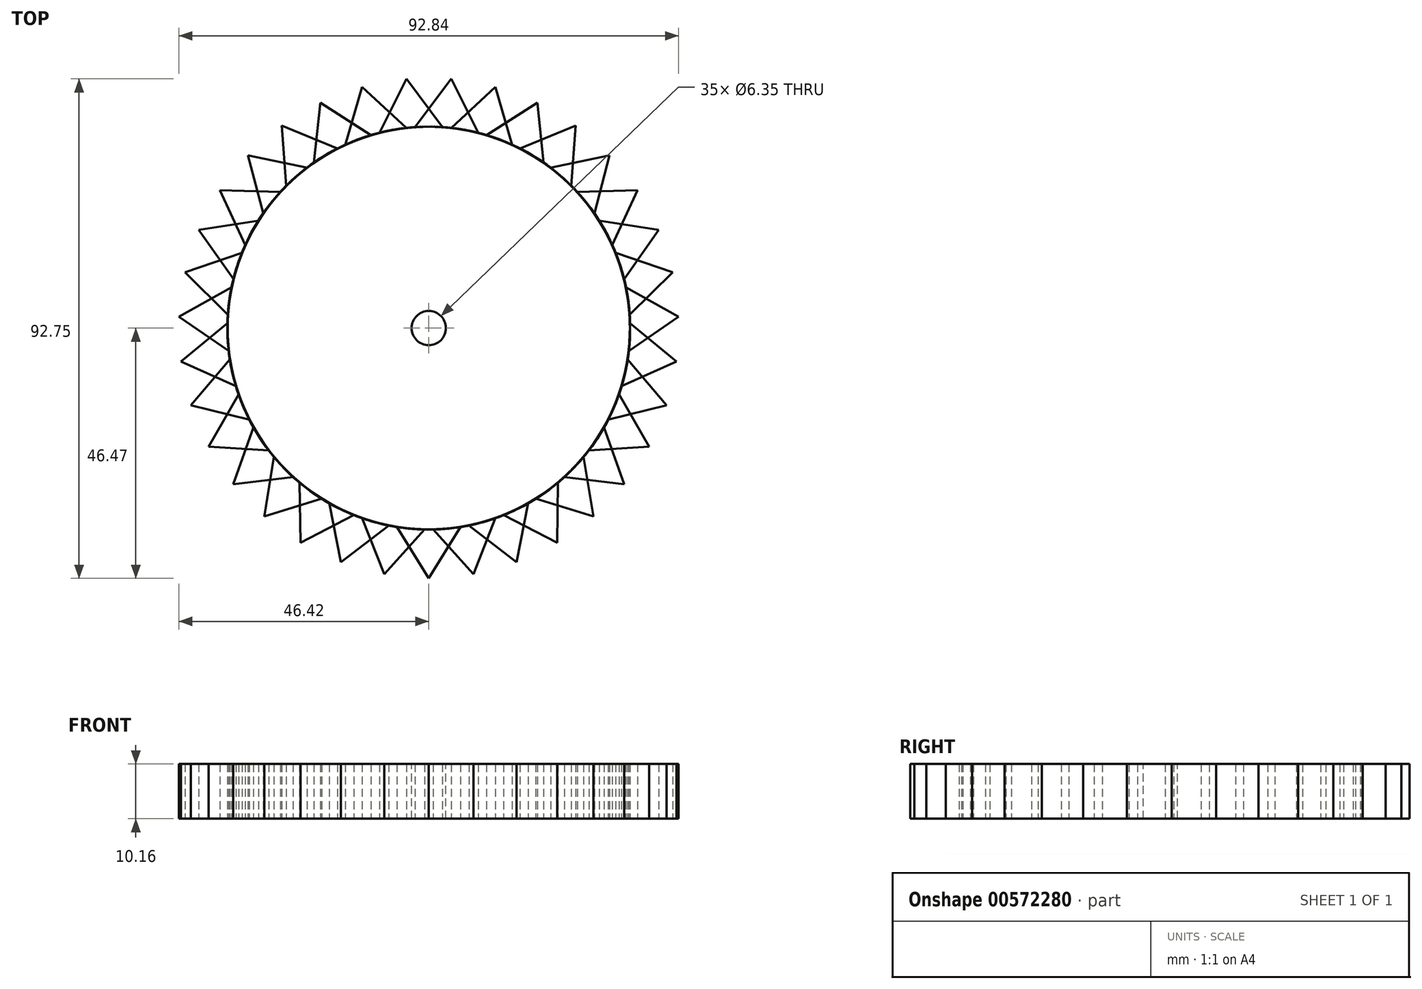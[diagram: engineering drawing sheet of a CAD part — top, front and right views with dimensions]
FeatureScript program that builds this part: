
annotation { "Feature Type Name" : "Feature", "Feature Type Description" : "" }
export const myFeature = defineFeature(function(context is Context, id is Id, definition is map)
    precondition{}
    {
        {
            var Q0;
            Q0=qCreatedBy(makeId("Top.planeOp"),FACE);
            var sketch = newSketch(context, id + "F0", { "sketchPlane" : qUnion([Q0])});
            skCircle(sketch, "E0", {"center": v(0, 0) * mm, "radius": 37.42 * mm});
            skLineSegment(sketch, "E1", {"start": v(0, -37.42) * mm, "end": v(0, -46.47) * mm});
            skLineSegment(sketch, "E2", {"start": v(0, -46.47) * mm, "end": v(5.89, -36.95) * mm});
            skLineSegment(sketch, "E3", {"start": v(0, -46.47) * mm, "end": v(-5.89, -36.95) * mm});
            skSolve(sketch);
        }
        {
            var Q0;
            {var subQ0=sQuery(id+"F0.wireOp",EDGE,"E0");var subQ1=makeQuery(id+"F0.imprint","INTERSECT",VERTEX,{"derivedFrom":[subQ0,sQuery(id+"F0.wireOp",EDGE,"E1")]});Q0=makeQuery(id+"F0.imprint","IMPRINT",FACE,{"disambiguationData":[TD([[makeQuery(id+"F0.imprint","IMPRINT",EDGE,{"disambiguationData":[TD([[subQ1,1.0]])],"derivedFrom":subQ0}),1.0]])]});}
            var Q1;
            {var subQ0=sQuery(id+"F0.wireOp",EDGE,"E1");Q1=makeQuery(id+"F0.imprint","IMPRINT",FACE,{"disambiguationData":[TD([[makeQuery(id+"F0.imprint","IMPRINT",EDGE,{"derivedFrom":subQ0}),1.0]])]});}
            var Q2;
            {var subQ0=sQuery(id+"F0.wireOp",EDGE,"E1");Q2=makeQuery(id+"F0.imprint","IMPRINT",FACE,{"disambiguationData":[TD([[makeQuery(id+"F0.imprint","IMPRINT",EDGE,{"derivedFrom":subQ0}),-1.0]])]});}
            extrude(context, id + "F1", {"entities" : qUnion([Q0, Q1, Q2]), "depth" : 10.16 * mm, "offsetDistance" : 25.4 * mm});
        }
        {
            var Q0;
            Q0=makeQuery(id+"F1.opExtrude","SWEPT_BODY",BODY,{"disambiguationData":[OSD([sQuery(id+"F0.wireOp",EDGE,"E0"),sQuery(id+"F0.wireOp",EDGE,"E2"),sQuery(id+"F0.wireOp",EDGE,"E3")])]});
            var Q1;
            Q1=makeQuery(id+"F1.opExtrude","CAP_EDGE",EDGE,{"disambiguationData":[OSD([sQuery(id+"F0.wireOp",EDGE,"E0")])],"isStart":true});
            circularPattern(context, id + "F2", {"entities" : qUnion([Q0]), "axis" : qUnion([Q1]), "angle" : 360 * degree, "instanceCount" : 35, "equalSpace" : true});
        }
        {
            var Q0;
            Q0=makeQuery(id+"F2.opPattern","COPY",FACE,{"derivedFrom":makeQuery(id+"F1.opExtrude","CAP_FACE",FACE,{"disambiguationData":[OSD([sQuery(id+"F0.wireOp",EDGE,"E0"),sQuery(id+"F0.wireOp",EDGE,"E2"),sQuery(id+"F0.wireOp",EDGE,"E3")])],"isStart":false}),"instanceName":"12"});
            var sketch = newSketch(context, id + "F3", { "sketchPlane" : qUnion([Q0])});
            skPoint(sketch, "E4", {"position": v(0, 0) * mm});
            skSolve(sketch);
        }
        {
            var Q0;
            Q0=sQuery(id+"F3.wireOp",VERTEX,"E4");
            var Q1;
            Q1=makeQuery(id+"F1.opExtrude","SWEPT_BODY",BODY,{"disambiguationData":[OSD([sQuery(id+"F0.wireOp",EDGE,"E0"),sQuery(id+"F0.wireOp",EDGE,"E2"),sQuery(id+"F0.wireOp",EDGE,"E3")])]});
            var Q2;
            Q2=makeQuery(id+"F2.opPattern","COPY",BODY,{"derivedFrom":makeQuery(id+"F1.opExtrude","SWEPT_BODY",BODY,{"disambiguationData":[OSD([sQuery(id+"F0.wireOp",EDGE,"E0"),sQuery(id+"F0.wireOp",EDGE,"E2"),sQuery(id+"F0.wireOp",EDGE,"E3")])]}),"instanceName":"1"});
            var Q3;
            Q3=makeQuery(id+"F2.opPattern","COPY",BODY,{"derivedFrom":makeQuery(id+"F1.opExtrude","SWEPT_BODY",BODY,{"disambiguationData":[OSD([sQuery(id+"F0.wireOp",EDGE,"E0"),sQuery(id+"F0.wireOp",EDGE,"E2"),sQuery(id+"F0.wireOp",EDGE,"E3")])]}),"instanceName":"2"});
            var Q4;
            Q4=makeQuery(id+"F2.opPattern","COPY",BODY,{"derivedFrom":makeQuery(id+"F1.opExtrude","SWEPT_BODY",BODY,{"disambiguationData":[OSD([sQuery(id+"F0.wireOp",EDGE,"E0"),sQuery(id+"F0.wireOp",EDGE,"E2"),sQuery(id+"F0.wireOp",EDGE,"E3")])]}),"instanceName":"3"});
            var Q5;
            Q5=makeQuery(id+"F2.opPattern","COPY",BODY,{"derivedFrom":makeQuery(id+"F1.opExtrude","SWEPT_BODY",BODY,{"disambiguationData":[OSD([sQuery(id+"F0.wireOp",EDGE,"E0"),sQuery(id+"F0.wireOp",EDGE,"E2"),sQuery(id+"F0.wireOp",EDGE,"E3")])]}),"instanceName":"4"});
            var Q6;
            Q6=makeQuery(id+"F2.opPattern","COPY",BODY,{"derivedFrom":makeQuery(id+"F1.opExtrude","SWEPT_BODY",BODY,{"disambiguationData":[OSD([sQuery(id+"F0.wireOp",EDGE,"E0"),sQuery(id+"F0.wireOp",EDGE,"E2"),sQuery(id+"F0.wireOp",EDGE,"E3")])]}),"instanceName":"5"});
            var Q7;
            Q7=makeQuery(id+"F2.opPattern","COPY",BODY,{"derivedFrom":makeQuery(id+"F1.opExtrude","SWEPT_BODY",BODY,{"disambiguationData":[OSD([sQuery(id+"F0.wireOp",EDGE,"E0"),sQuery(id+"F0.wireOp",EDGE,"E2"),sQuery(id+"F0.wireOp",EDGE,"E3")])]}),"instanceName":"6"});
            var Q8;
            Q8=makeQuery(id+"F2.opPattern","COPY",BODY,{"derivedFrom":makeQuery(id+"F1.opExtrude","SWEPT_BODY",BODY,{"disambiguationData":[OSD([sQuery(id+"F0.wireOp",EDGE,"E0"),sQuery(id+"F0.wireOp",EDGE,"E2"),sQuery(id+"F0.wireOp",EDGE,"E3")])]}),"instanceName":"7"});
            var Q9;
            Q9=makeQuery(id+"F2.opPattern","COPY",BODY,{"derivedFrom":makeQuery(id+"F1.opExtrude","SWEPT_BODY",BODY,{"disambiguationData":[OSD([sQuery(id+"F0.wireOp",EDGE,"E0"),sQuery(id+"F0.wireOp",EDGE,"E2"),sQuery(id+"F0.wireOp",EDGE,"E3")])]}),"instanceName":"8"});
            var Q10;
            Q10=makeQuery(id+"F2.opPattern","COPY",BODY,{"derivedFrom":makeQuery(id+"F1.opExtrude","SWEPT_BODY",BODY,{"disambiguationData":[OSD([sQuery(id+"F0.wireOp",EDGE,"E0"),sQuery(id+"F0.wireOp",EDGE,"E2"),sQuery(id+"F0.wireOp",EDGE,"E3")])]}),"instanceName":"9"});
            var Q11;
            Q11=makeQuery(id+"F2.opPattern","COPY",BODY,{"derivedFrom":makeQuery(id+"F1.opExtrude","SWEPT_BODY",BODY,{"disambiguationData":[OSD([sQuery(id+"F0.wireOp",EDGE,"E0"),sQuery(id+"F0.wireOp",EDGE,"E2"),sQuery(id+"F0.wireOp",EDGE,"E3")])]}),"instanceName":"10"});
            var Q12;
            Q12=makeQuery(id+"F2.opPattern","COPY",BODY,{"derivedFrom":makeQuery(id+"F1.opExtrude","SWEPT_BODY",BODY,{"disambiguationData":[OSD([sQuery(id+"F0.wireOp",EDGE,"E0"),sQuery(id+"F0.wireOp",EDGE,"E2"),sQuery(id+"F0.wireOp",EDGE,"E3")])]}),"instanceName":"11"});
            var Q13;
            Q13=makeQuery(id+"F2.opPattern","COPY",BODY,{"derivedFrom":makeQuery(id+"F1.opExtrude","SWEPT_BODY",BODY,{"disambiguationData":[OSD([sQuery(id+"F0.wireOp",EDGE,"E0"),sQuery(id+"F0.wireOp",EDGE,"E2"),sQuery(id+"F0.wireOp",EDGE,"E3")])]}),"instanceName":"12"});
            var Q14;
            Q14=makeQuery(id+"F2.opPattern","COPY",BODY,{"derivedFrom":makeQuery(id+"F1.opExtrude","SWEPT_BODY",BODY,{"disambiguationData":[OSD([sQuery(id+"F0.wireOp",EDGE,"E0"),sQuery(id+"F0.wireOp",EDGE,"E2"),sQuery(id+"F0.wireOp",EDGE,"E3")])]}),"instanceName":"13"});
            var Q15;
            Q15=makeQuery(id+"F2.opPattern","COPY",BODY,{"derivedFrom":makeQuery(id+"F1.opExtrude","SWEPT_BODY",BODY,{"disambiguationData":[OSD([sQuery(id+"F0.wireOp",EDGE,"E0"),sQuery(id+"F0.wireOp",EDGE,"E2"),sQuery(id+"F0.wireOp",EDGE,"E3")])]}),"instanceName":"14"});
            var Q16;
            Q16=makeQuery(id+"F2.opPattern","COPY",BODY,{"derivedFrom":makeQuery(id+"F1.opExtrude","SWEPT_BODY",BODY,{"disambiguationData":[OSD([sQuery(id+"F0.wireOp",EDGE,"E0"),sQuery(id+"F0.wireOp",EDGE,"E2"),sQuery(id+"F0.wireOp",EDGE,"E3")])]}),"instanceName":"15"});
            var Q17;
            Q17=makeQuery(id+"F2.opPattern","COPY",BODY,{"derivedFrom":makeQuery(id+"F1.opExtrude","SWEPT_BODY",BODY,{"disambiguationData":[OSD([sQuery(id+"F0.wireOp",EDGE,"E0"),sQuery(id+"F0.wireOp",EDGE,"E2"),sQuery(id+"F0.wireOp",EDGE,"E3")])]}),"instanceName":"16"});
            var Q18;
            Q18=makeQuery(id+"F2.opPattern","COPY",BODY,{"derivedFrom":makeQuery(id+"F1.opExtrude","SWEPT_BODY",BODY,{"disambiguationData":[OSD([sQuery(id+"F0.wireOp",EDGE,"E0"),sQuery(id+"F0.wireOp",EDGE,"E2"),sQuery(id+"F0.wireOp",EDGE,"E3")])]}),"instanceName":"17"});
            var Q19;
            Q19=makeQuery(id+"F2.opPattern","COPY",BODY,{"derivedFrom":makeQuery(id+"F1.opExtrude","SWEPT_BODY",BODY,{"disambiguationData":[OSD([sQuery(id+"F0.wireOp",EDGE,"E0"),sQuery(id+"F0.wireOp",EDGE,"E2"),sQuery(id+"F0.wireOp",EDGE,"E3")])]}),"instanceName":"18"});
            var Q20;
            Q20=makeQuery(id+"F2.opPattern","COPY",BODY,{"derivedFrom":makeQuery(id+"F1.opExtrude","SWEPT_BODY",BODY,{"disambiguationData":[OSD([sQuery(id+"F0.wireOp",EDGE,"E0"),sQuery(id+"F0.wireOp",EDGE,"E2"),sQuery(id+"F0.wireOp",EDGE,"E3")])]}),"instanceName":"19"});
            var Q21;
            Q21=makeQuery(id+"F2.opPattern","COPY",BODY,{"derivedFrom":makeQuery(id+"F1.opExtrude","SWEPT_BODY",BODY,{"disambiguationData":[OSD([sQuery(id+"F0.wireOp",EDGE,"E0"),sQuery(id+"F0.wireOp",EDGE,"E2"),sQuery(id+"F0.wireOp",EDGE,"E3")])]}),"instanceName":"20"});
            var Q22;
            Q22=makeQuery(id+"F2.opPattern","COPY",BODY,{"derivedFrom":makeQuery(id+"F1.opExtrude","SWEPT_BODY",BODY,{"disambiguationData":[OSD([sQuery(id+"F0.wireOp",EDGE,"E0"),sQuery(id+"F0.wireOp",EDGE,"E2"),sQuery(id+"F0.wireOp",EDGE,"E3")])]}),"instanceName":"21"});
            var Q23;
            Q23=makeQuery(id+"F2.opPattern","COPY",BODY,{"derivedFrom":makeQuery(id+"F1.opExtrude","SWEPT_BODY",BODY,{"disambiguationData":[OSD([sQuery(id+"F0.wireOp",EDGE,"E0"),sQuery(id+"F0.wireOp",EDGE,"E2"),sQuery(id+"F0.wireOp",EDGE,"E3")])]}),"instanceName":"22"});
            var Q24;
            Q24=makeQuery(id+"F2.opPattern","COPY",BODY,{"derivedFrom":makeQuery(id+"F1.opExtrude","SWEPT_BODY",BODY,{"disambiguationData":[OSD([sQuery(id+"F0.wireOp",EDGE,"E0"),sQuery(id+"F0.wireOp",EDGE,"E2"),sQuery(id+"F0.wireOp",EDGE,"E3")])]}),"instanceName":"23"});
            var Q25;
            Q25=makeQuery(id+"F2.opPattern","COPY",BODY,{"derivedFrom":makeQuery(id+"F1.opExtrude","SWEPT_BODY",BODY,{"disambiguationData":[OSD([sQuery(id+"F0.wireOp",EDGE,"E0"),sQuery(id+"F0.wireOp",EDGE,"E2"),sQuery(id+"F0.wireOp",EDGE,"E3")])]}),"instanceName":"24"});
            var Q26;
            Q26=makeQuery(id+"F2.opPattern","COPY",BODY,{"derivedFrom":makeQuery(id+"F1.opExtrude","SWEPT_BODY",BODY,{"disambiguationData":[OSD([sQuery(id+"F0.wireOp",EDGE,"E0"),sQuery(id+"F0.wireOp",EDGE,"E2"),sQuery(id+"F0.wireOp",EDGE,"E3")])]}),"instanceName":"25"});
            var Q27;
            Q27=makeQuery(id+"F2.opPattern","COPY",BODY,{"derivedFrom":makeQuery(id+"F1.opExtrude","SWEPT_BODY",BODY,{"disambiguationData":[OSD([sQuery(id+"F0.wireOp",EDGE,"E0"),sQuery(id+"F0.wireOp",EDGE,"E2"),sQuery(id+"F0.wireOp",EDGE,"E3")])]}),"instanceName":"26"});
            var Q28;
            Q28=makeQuery(id+"F2.opPattern","COPY",BODY,{"derivedFrom":makeQuery(id+"F1.opExtrude","SWEPT_BODY",BODY,{"disambiguationData":[OSD([sQuery(id+"F0.wireOp",EDGE,"E0"),sQuery(id+"F0.wireOp",EDGE,"E2"),sQuery(id+"F0.wireOp",EDGE,"E3")])]}),"instanceName":"27"});
            var Q29;
            Q29=makeQuery(id+"F2.opPattern","COPY",BODY,{"derivedFrom":makeQuery(id+"F1.opExtrude","SWEPT_BODY",BODY,{"disambiguationData":[OSD([sQuery(id+"F0.wireOp",EDGE,"E0"),sQuery(id+"F0.wireOp",EDGE,"E2"),sQuery(id+"F0.wireOp",EDGE,"E3")])]}),"instanceName":"28"});
            var Q30;
            Q30=makeQuery(id+"F2.opPattern","COPY",BODY,{"derivedFrom":makeQuery(id+"F1.opExtrude","SWEPT_BODY",BODY,{"disambiguationData":[OSD([sQuery(id+"F0.wireOp",EDGE,"E0"),sQuery(id+"F0.wireOp",EDGE,"E2"),sQuery(id+"F0.wireOp",EDGE,"E3")])]}),"instanceName":"29"});
            var Q31;
            Q31=makeQuery(id+"F2.opPattern","COPY",BODY,{"derivedFrom":makeQuery(id+"F1.opExtrude","SWEPT_BODY",BODY,{"disambiguationData":[OSD([sQuery(id+"F0.wireOp",EDGE,"E0"),sQuery(id+"F0.wireOp",EDGE,"E2"),sQuery(id+"F0.wireOp",EDGE,"E3")])]}),"instanceName":"30"});
            var Q32;
            Q32=makeQuery(id+"F2.opPattern","COPY",BODY,{"derivedFrom":makeQuery(id+"F1.opExtrude","SWEPT_BODY",BODY,{"disambiguationData":[OSD([sQuery(id+"F0.wireOp",EDGE,"E0"),sQuery(id+"F0.wireOp",EDGE,"E2"),sQuery(id+"F0.wireOp",EDGE,"E3")])]}),"instanceName":"31"});
            var Q33;
            Q33=makeQuery(id+"F2.opPattern","COPY",BODY,{"derivedFrom":makeQuery(id+"F1.opExtrude","SWEPT_BODY",BODY,{"disambiguationData":[OSD([sQuery(id+"F0.wireOp",EDGE,"E0"),sQuery(id+"F0.wireOp",EDGE,"E2"),sQuery(id+"F0.wireOp",EDGE,"E3")])]}),"instanceName":"32"});
            var Q34;
            Q34=makeQuery(id+"F2.opPattern","COPY",BODY,{"derivedFrom":makeQuery(id+"F1.opExtrude","SWEPT_BODY",BODY,{"disambiguationData":[OSD([sQuery(id+"F0.wireOp",EDGE,"E0"),sQuery(id+"F0.wireOp",EDGE,"E2"),sQuery(id+"F0.wireOp",EDGE,"E3")])]}),"instanceName":"33"});
            var Q35;
            Q35=makeQuery(id+"F2.opPattern","COPY",BODY,{"derivedFrom":makeQuery(id+"F1.opExtrude","SWEPT_BODY",BODY,{"disambiguationData":[OSD([sQuery(id+"F0.wireOp",EDGE,"E0"),sQuery(id+"F0.wireOp",EDGE,"E2"),sQuery(id+"F0.wireOp",EDGE,"E3")])]}),"instanceName":"34"});
            var Q36;
            Q36=makeQuery(id+"F2.opPattern","COPY",BODY,{"derivedFrom":makeQuery(id+"F1.opExtrude","SWEPT_BODY",BODY,{"disambiguationData":[OSD([sQuery(id+"F0.wireOp",EDGE,"E0"),sQuery(id+"F0.wireOp",EDGE,"E2"),sQuery(id+"F0.wireOp",EDGE,"E3")])]}),"instanceName":"35"});
            var Q37;
            Q37=makeQuery(id+"F2.opPattern","COPY",BODY,{"derivedFrom":makeQuery(id+"F1.opExtrude","SWEPT_BODY",BODY,{"disambiguationData":[OSD([sQuery(id+"F0.wireOp",EDGE,"E0"),sQuery(id+"F0.wireOp",EDGE,"E2"),sQuery(id+"F0.wireOp",EDGE,"E3")])]}),"instanceName":"36"});
            var Q38;
            Q38=makeQuery(id+"F2.opPattern","COPY",BODY,{"derivedFrom":makeQuery(id+"F1.opExtrude","SWEPT_BODY",BODY,{"disambiguationData":[OSD([sQuery(id+"F0.wireOp",EDGE,"E0"),sQuery(id+"F0.wireOp",EDGE,"E2"),sQuery(id+"F0.wireOp",EDGE,"E3")])]}),"instanceName":"37"});
            var Q39;
            Q39=makeQuery(id+"F2.opPattern","COPY",BODY,{"derivedFrom":makeQuery(id+"F1.opExtrude","SWEPT_BODY",BODY,{"disambiguationData":[OSD([sQuery(id+"F0.wireOp",EDGE,"E0"),sQuery(id+"F0.wireOp",EDGE,"E2"),sQuery(id+"F0.wireOp",EDGE,"E3")])]}),"instanceName":"38"});
            var Q40;
            Q40=makeQuery(id+"F2.opPattern","COPY",BODY,{"derivedFrom":makeQuery(id+"F1.opExtrude","SWEPT_BODY",BODY,{"disambiguationData":[OSD([sQuery(id+"F0.wireOp",EDGE,"E0"),sQuery(id+"F0.wireOp",EDGE,"E2"),sQuery(id+"F0.wireOp",EDGE,"E3")])]}),"instanceName":"39"});
            var Q41;
            Q41=makeQuery(id+"F2.opPattern","COPY",BODY,{"derivedFrom":makeQuery(id+"F1.opExtrude","SWEPT_BODY",BODY,{"disambiguationData":[OSD([sQuery(id+"F0.wireOp",EDGE,"E0"),sQuery(id+"F0.wireOp",EDGE,"E2"),sQuery(id+"F0.wireOp",EDGE,"E3")])]}),"instanceName":"40"});
            var Q42;
            Q42=makeQuery(id+"F2.opPattern","COPY",BODY,{"derivedFrom":makeQuery(id+"F1.opExtrude","SWEPT_BODY",BODY,{"disambiguationData":[OSD([sQuery(id+"F0.wireOp",EDGE,"E0"),sQuery(id+"F0.wireOp",EDGE,"E2"),sQuery(id+"F0.wireOp",EDGE,"E3")])]}),"instanceName":"41"});
            var Q43;
            Q43=makeQuery(id+"F2.opPattern","COPY",BODY,{"derivedFrom":makeQuery(id+"F1.opExtrude","SWEPT_BODY",BODY,{"disambiguationData":[OSD([sQuery(id+"F0.wireOp",EDGE,"E0"),sQuery(id+"F0.wireOp",EDGE,"E2"),sQuery(id+"F0.wireOp",EDGE,"E3")])]}),"instanceName":"42"});
            var Q44;
            Q44=makeQuery(id+"F2.opPattern","COPY",BODY,{"derivedFrom":makeQuery(id+"F1.opExtrude","SWEPT_BODY",BODY,{"disambiguationData":[OSD([sQuery(id+"F0.wireOp",EDGE,"E0"),sQuery(id+"F0.wireOp",EDGE,"E2"),sQuery(id+"F0.wireOp",EDGE,"E3")])]}),"instanceName":"43"});
            var Q45;
            Q45=makeQuery(id+"F2.opPattern","COPY",BODY,{"derivedFrom":makeQuery(id+"F1.opExtrude","SWEPT_BODY",BODY,{"disambiguationData":[OSD([sQuery(id+"F0.wireOp",EDGE,"E0"),sQuery(id+"F0.wireOp",EDGE,"E2"),sQuery(id+"F0.wireOp",EDGE,"E3")])]}),"instanceName":"44"});
            hole(context, id + "F4", {"style" : HoleStyle.SIMPLE, "endStyle" : HoleEndStyle.THROUGH, "holeDiameter" : 6.35 * mm, "isTappedThrough" : true, "tappedDepth" : 12.7 * mm, "tapClearance" : 3, "locations" : qUnion([Q0]), "scope" : qUnion([Q1, Q2, Q3, Q4, Q5, Q6, Q7, Q8, Q9, Q10, Q11, Q12, Q13, Q14, Q15, Q16, Q17, Q18, Q19, Q20, Q21, Q22, Q23, Q24, Q25, Q26, Q27, Q28, Q29, Q30, Q31, Q32, Q33, Q34, Q35, Q36, Q37, Q38, Q39, Q40, Q41, Q42, Q43, Q44, Q45])});
        }
    });
